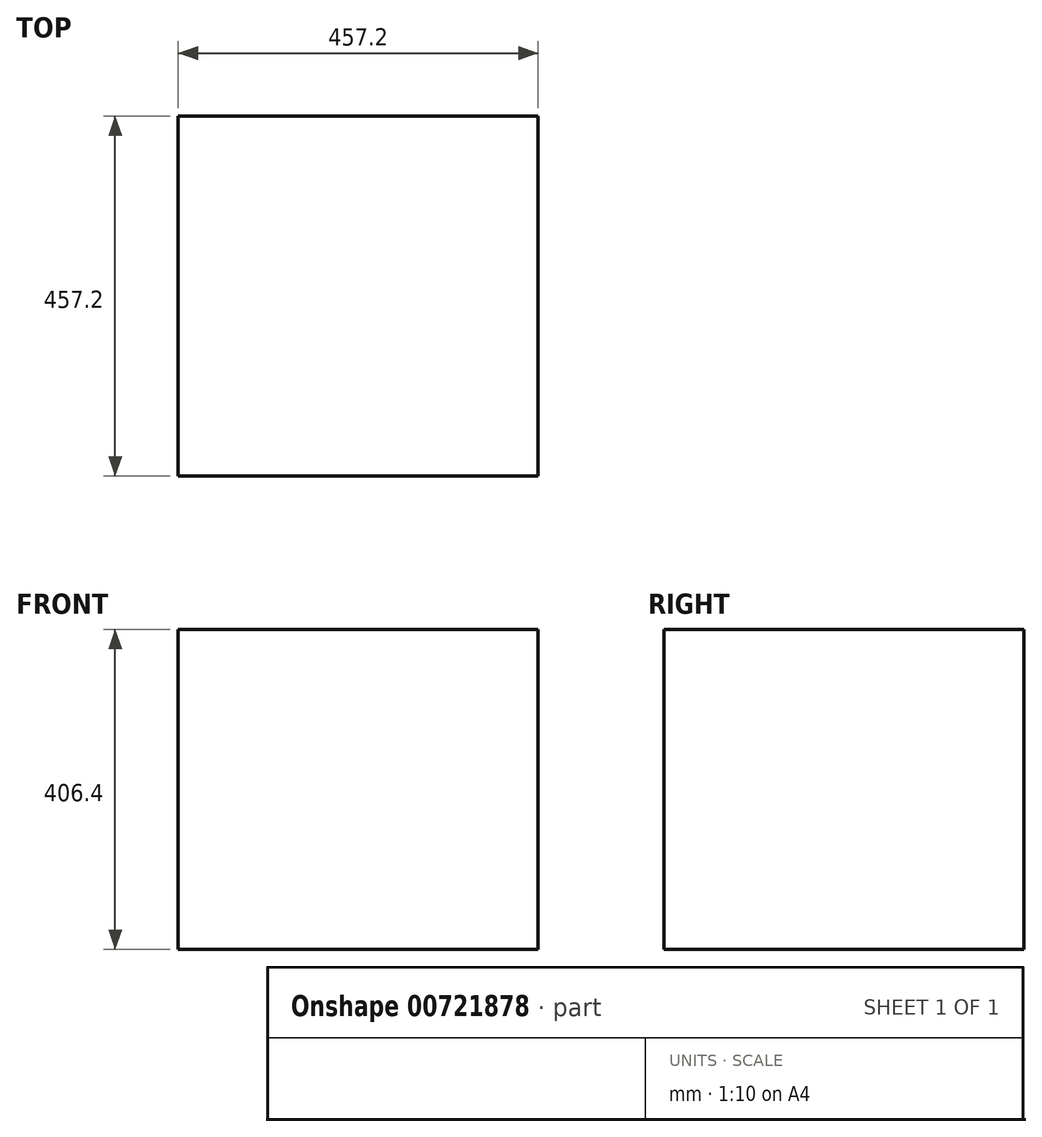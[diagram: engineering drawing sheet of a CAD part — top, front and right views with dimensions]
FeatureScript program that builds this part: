
annotation { "Feature Type Name" : "Feature", "Feature Type Description" : "" }
export const myFeature = defineFeature(function(context is Context, id is Id, definition is map)
    precondition{}
    {
        {
            var Q0;
            Q0=qCreatedBy(makeId("Front.planeOp"),FACE);
            var sketch = newSketch(context, id + "F0", { "sketchPlane" : qUnion([Q0])});
            skLineSegment(sketch, "E0.bottom", {"start": v(-464, 89.13) * mm, "end": v(-6.8, 89.13) * mm});
            skLineSegment(sketch, "E0.top", {"start": v(-464, -317.27) * mm, "end": v(-6.8, -317.27) * mm});
            skLineSegment(sketch, "E0.left", {"start": v(-464, 89.13) * mm, "end": v(-464, -317.27) * mm});
            skLineSegment(sketch, "E0.right", {"start": v(-6.8, 89.13) * mm, "end": v(-6.8, -317.27) * mm});
            skSolve(sketch);
        }
        {
            var Q0;
            Q0=makeQuery(id+"F0.imprint","IMPRINT",FACE,{"disambiguationData":[TD([[makeQuery(id+"F0.imprint","IMPRINT",EDGE,{"derivedFrom":sQuery(id+"F0.wireOp",EDGE,"E0.bottom")}),-1.0]])]});
            extrude(context, id + "F1", {"entities" : qUnion([Q0]), "depth" : 457.2 * mm, "offsetDistance" : 25.4 * mm});
        }
    });
